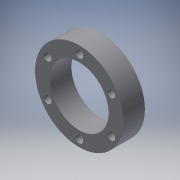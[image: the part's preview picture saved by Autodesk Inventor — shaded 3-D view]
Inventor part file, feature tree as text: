
AUTODESK INVENTOR PART (.ipt)
format: ipt  version: 2016 (Build 200138000, 138)  size: 122,368 bytes
history: native  units: in
note: dims shown in document units (in); Inventor stores cm internally (conversion verified against a paired STEP export)
features: extrude x1, sketch x1
ambient origin geometry x8: Origin, YZ Plane, XZ Plane, XY Plane, X Axis, Y Axis, Z Axis, Center Point
bodies: Solid1 (feature_tree)
feature tree (2):
  extrude  "Extrusion1"  Depth=0.55in
  sketch  "Sketch1"  dims[d0=2.25in d1=1.875in d2=0.204in d3=0.204in d4=0.204in d5=0.204in d6=0.204in d7=0.204in d8=1.5in d9=0.55in d10=0.0in]
